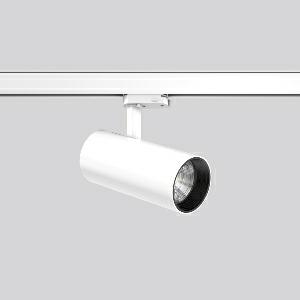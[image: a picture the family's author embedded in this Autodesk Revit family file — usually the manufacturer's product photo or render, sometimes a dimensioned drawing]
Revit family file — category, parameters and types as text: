
# Revit family: deecos_s_mini_742200_002_76_8dc2
name_source: partatom
category: Lighting Fixtures
units: mm (PartAtom-declared; Revit-internal decimal feet)

## family parameters
Cut with Voids When Loaded = No
Host = Face
Light Source = No
Part Type = Normal
Room Calculation Point = No
Round Connector Dimension = Use Diameter
Shared = No

## types (1)
- DEECOS S mini (1 x LED Modul 930, 2000 lm, 3000)
    Apparent Load = 20 VA
    Approval mark = CE
    CIE Flux Codes = 98 100 100 100 100
    Color Rendering = 90
    Color Temperature = 3000
    Default Elevation = 1800 mm
    Description = Series: DEECOS S mini
LED surface-mounted projector in modern design with no visible cooling ribs. Housing: die-cast aluminium, powder-coated. Rotation range: 356°. Swivel range: 90°. Black plastic ring and recessed LED to prevent glare from the side. Optical assembly with lens made of plastic (polycarbonate) for the best homogeneous light distribution - can be changed without tools. Best colour rendering index Ra>90. With adapter for RZB 3-circuit DALI tracks. Suitable for Track on ceiling, Wall track. High quality converter without flickering and stroboscopic effect. The following accessories can be mounted without use of tools: interchangeable lenses, decorative glasses, honeycomb louvre, clear and frosted diffusers, white interchangeable plastic ring. 
Colour: traffic white, matt (RAL 9016)
Diameter: 87 mm
Height: 214 mm
Lamp: LED
Socket: without socket
Colour temperature: 3000K
Colour rendering index (CRI): 92
System power: 20 W
Rated luminous flux: 2000 lm
Luminous efficiency: 100 lm/W
Control gear: Converter, dimmable, DALI
Protection class: I
Type of protection: IP 20
    Height = 214 mm
    Lamp = 1 x LED Modul 930
    Lamp Light Flux = 2000 lm
    Lamp count = 1
    Length = 87 mm
    Lifetime = 50000 h
    Luminous efficacy = 100 lm/W
    Manufacturer = RZB
    ModVariant = No
    Model = 742200.002.76
    Mounting Place = Ceiling
    Mounting Type = Rail mounted
    Number of Poles = 1
    OnlyDefault = Yes
    Power Factor = 1
    Product Name = DEECOS S mini
    Product group = Track mounted projectors
    ProductGroupID = 301
    Protection Class = Protection class I
    Protection Degree = IP 20
    RLX_Detail_Level = 1
    RLX_Emergency_Light_Flux = 0 lm
    RLX_Emergency_Type = 0
    RLX_Emergency_Type_DB = No
    RlxData = <blob elided: 35305 chars, md5=7599e330>
    Socket = socket
    Standby Power = 0 W
    System Light Flux = 2000 lm
    System Power = 20 W
    Type Comments = Product without accessories
    Type Image = 741930.002.jpg
    URL = http://relux.com
    VarID = ---
    Voltage = 230 V
    Voltage Range = 220-240 V
    Weight = 0.00 kg
    Width = 0 mm  [stored 0 ft]

note: [stored X ft] marks values corroborated as IEEE doubles in the binary element streams (Revit-internal decimal feet)

## geometry (parser evidence)
native form markers: Blend x4, Sweep x13
no freeform markers — native parametric forms only
